# Revit family: new
name_source: partatom
category: Lighting Fixtures
revit_build: Autodesk Revit 2014 (Build: 20130308_1515(x64)
units: mm (PartAtom-declared; Revit-internal decimal feet)

## types (1)
- LF6ML
    Apparent Load = 0 VA
    Assembly Code = D5020200
    Backbox = Paint-Hubbell-White
    Color Filter = 16777215
    Default Elevation = 48.000"
    Description = Designed for optimal life and lumen maintenance, the LF6 is a 6 inch architectural LED downlight with color consistency from fixture to fixture.
    Dimming Lamp Color Temperature Shift = <None>
    Emit Shape Visible in Rendering = No
    Emit from Circle Diameter = 5.500"
    Features = Light Engine utilizes Philips Fortimo LED module and provides controlled color consistency
Universal 120-277V high efficiency LED driver with 0-10V dimming standard
1100, 1500, 2000, and 3000 lumen modules
Photometrics tested per IESNA-LM-79-2008 standards
Minimum 50,000 hours at 70% lumen maintenance
5-year warranty
Clear or Diffuse regressed lens option available with multiple colors and trim options.
SpectraSync™ Color Tuning Technology available
NX Distributed Intelligence™ wired and wireless controls capability available
    Glass = Glass
    Is 120V = Yes
    Is 277V = No
    Lamp = LED
    Load Classification = Lighting
    Manufacturer = Healthcare Solutions
    Model = LF6
    Mounting = Recessed
    Photometric Web File = generic.ies
    Product Documentation Link = https://hubbellcdn.com
    Product Page URL = https://www.hubbell.com
    Steel = Steel
    Tilt Angle = -90.00°
    Type Comments = Lighting Fixture
    URL = https://www.hubbell.com
    Voltage = 120 V
    Warranty = 5-Years Warranty
    Wattage Comments = 19W
    Wire = Wire

## geometry (parser evidence)
native form markers: Sweep x2
no freeform markers — native parametric forms only
